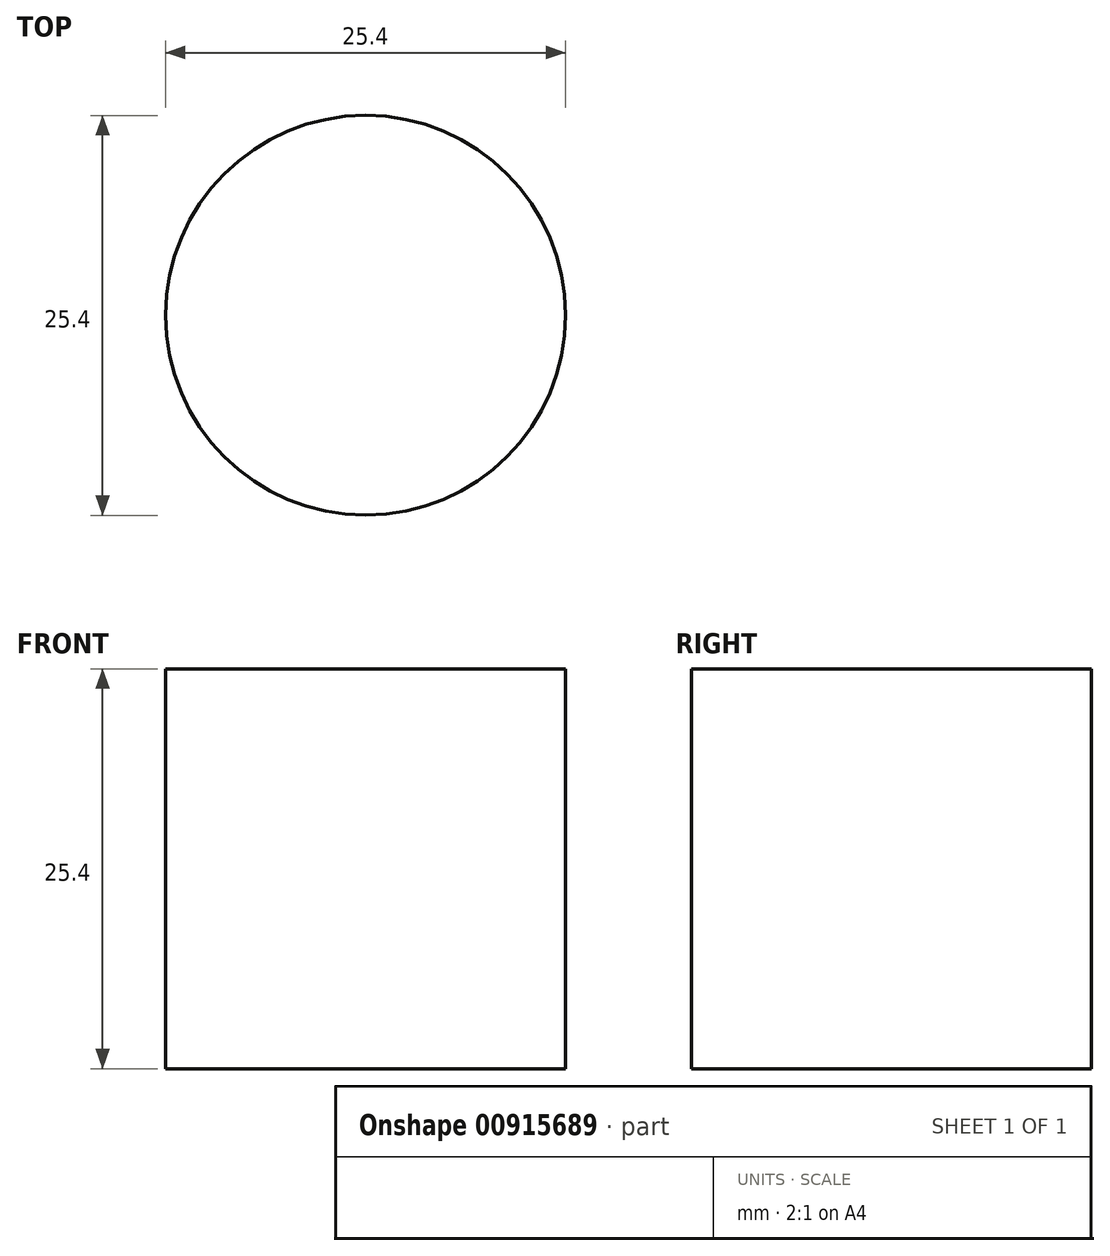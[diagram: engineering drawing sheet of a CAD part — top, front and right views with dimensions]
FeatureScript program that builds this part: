
annotation { "Feature Type Name" : "Feature", "Feature Type Description" : "" }
export const myFeature = defineFeature(function(context is Context, id is Id, definition is map)
    precondition{}
    {
        {
            var Q0;
            Q0=qCreatedBy(makeId("Top.planeOp"),FACE);
            var sketch = newSketch(context, id + "F0", { "sketchPlane" : qUnion([Q0])});
            skCircle(sketch, "E0", {"center": v(-119.73, -48.44) * mm, "radius": 12.7 * mm});
            skSolve(sketch);
        }
        {
            var Q0;
            Q0 = qSketchRegion(id + "F0", true);
            extrude(context, id + "F1", {"entities" : qUnion([Q0]), "depth" : 25.4 * mm, "offsetDistance" : 25.4 * mm});
        }
    });
